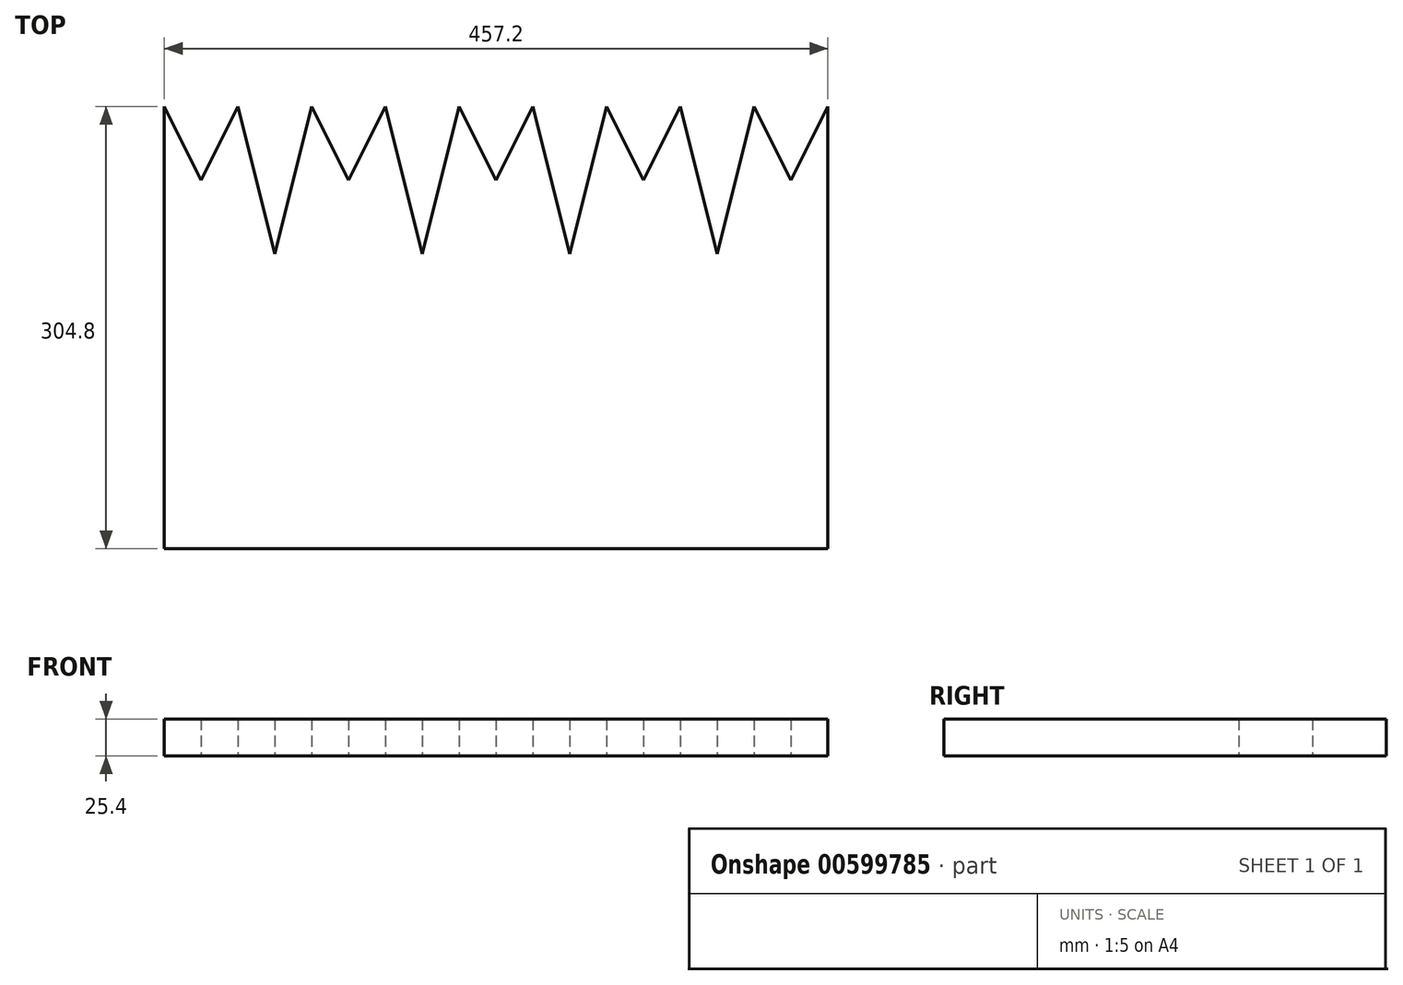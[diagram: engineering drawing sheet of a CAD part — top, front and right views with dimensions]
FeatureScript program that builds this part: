
annotation { "Feature Type Name" : "Feature", "Feature Type Description" : "" }
export const myFeature = defineFeature(function(context is Context, id is Id, definition is map)
    precondition{}
    {
        {
            var Q0;
            Q0=qCreatedBy(makeId("Top.planeOp"),FACE);
            var sketch = newSketch(context, id + "F0", { "sketchPlane" : qUnion([Q0])});
            skLineSegment(sketch, "E0.top", {"start": v(-261.46, -109.7) * mm, "end": v(195.74, -109.7) * mm});
            skLineSegment(sketch, "E0.left", {"start": v(-261.46, 195.1) * mm, "end": v(-261.46, -109.7) * mm});
            skLineSegment(sketch, "E0.right", {"start": v(195.74, 195.1) * mm, "end": v(195.74, -109.7) * mm});
            skLineSegment(sketch, "E1", {"start": v(-261.46, 144.3) * mm, "end": v(195.74, 144.3) * mm, "construction": true});
            skPoint(sketch, "E2", {"position": v(-236.06, 144.3) * mm});
            skPoint(sketch, "E3", {"position": v(-210.66, 144.3) * mm});
            skPoint(sketch, "E4", {"position": v(-185.26, 144.3) * mm});
            skPoint(sketch, "E5", {"position": v(-159.86, 144.3) * mm});
            skPoint(sketch, "E6", {"position": v(-134.46, 144.3) * mm});
            skPoint(sketch, "E7", {"position": v(-109.06, 144.3) * mm});
            skLineSegment(sketch, "E8", {"start": v(-32.86, 195.1) * mm, "end": v(-32.86, -109.7) * mm, "construction": true});
            skPoint(sketch, "E9", {"position": v(-83.66, 144.3) * mm});
            skPoint(sketch, "E10", {"position": v(-58.26, 144.3) * mm});
            skPoint(sketch, "E11.MirrorP", {"position": v(-7.46, 144.3) * mm});
            skPoint(sketch, "E12.MirrorP", {"position": v(17.94, 144.3) * mm});
            skPoint(sketch, "E13.MirrorP", {"position": v(43.34, 144.3) * mm});
            skPoint(sketch, "E14.MirrorP", {"position": v(68.74, 144.3) * mm});
            skPoint(sketch, "E15.MirrorP", {"position": v(94.14, 144.3) * mm});
            skPoint(sketch, "E16.MirrorP", {"position": v(119.54, 144.3) * mm});
            skPoint(sketch, "E17.MirrorP", {"position": v(144.94, 144.3) * mm});
            skPoint(sketch, "E18.MirrorP", {"position": v(170.34, 144.3) * mm});
            skPoint(sketch, "E19", {"position": v(-32.86, 144.3) * mm});
            skLineSegment(sketch, "E20", {"start": v(-261.46, 195.1) * mm, "end": v(-236.06, 144.3) * mm});
            skLineSegment(sketch, "E21", {"start": v(-210.66, 195.1) * mm, "end": v(-236.06, 144.3) * mm});
            skLineSegment(sketch, "E22", {"start": v(-159.86, 195.1) * mm, "end": v(-134.46, 144.3) * mm});
            skLineSegment(sketch, "E23", {"start": v(-134.46, 144.3) * mm, "end": v(-109.06, 195.1) * mm});
            skLineSegment(sketch, "E24", {"start": v(-58.26, 195.1) * mm, "end": v(-32.86, 144.3) * mm});
            skLineSegment(sketch, "E25", {"start": v(-32.86, 144.3) * mm, "end": v(-7.46, 195.1) * mm});
            skLineSegment(sketch, "E26", {"start": v(43.34, 195.1) * mm, "end": v(68.74, 144.3) * mm});
            skLineSegment(sketch, "E27", {"start": v(68.74, 144.3) * mm, "end": v(94.14, 195.1) * mm});
            skLineSegment(sketch, "E28", {"start": v(144.94, 195.1) * mm, "end": v(170.34, 144.3) * mm});
            skLineSegment(sketch, "E29", {"start": v(170.34, 144.3) * mm, "end": v(195.74, 195.1) * mm});
            skLineSegment(sketch, "E30", {"start": v(-261.46, 93.5) * mm, "end": v(195.74, 93.5) * mm, "construction": true});
            skLineSegment(sketch, "E31", {"start": v(-210.66, 195.1) * mm, "end": v(-185.26, 93.5) * mm});
            skLineSegment(sketch, "E32", {"start": v(-185.26, 93.5) * mm, "end": v(-159.86, 195.1) * mm});
            skLineSegment(sketch, "E33", {"start": v(-109.06, 195.1) * mm, "end": v(-83.66, 93.5) * mm});
            skLineSegment(sketch, "E34", {"start": v(-83.66, 93.5) * mm, "end": v(-58.26, 195.1) * mm});
            skLineSegment(sketch, "E35", {"start": v(-7.46, 195.1) * mm, "end": v(17.94, 93.5) * mm});
            skLineSegment(sketch, "E36", {"start": v(17.94, 93.5) * mm, "end": v(43.34, 195.1) * mm});
            skLineSegment(sketch, "E37", {"start": v(94.14, 195.1) * mm, "end": v(119.54, 93.5) * mm});
            skLineSegment(sketch, "E38", {"start": v(119.54, 93.5) * mm, "end": v(144.94, 195.1) * mm});
            skSolve(sketch);
        }
        {
            var Q0;
            Q0=makeQuery(id+"F0.imprint","IMPRINT",FACE,{"disambiguationData":[TD([[makeQuery(id+"F0.imprint","IMPRINT",EDGE,{"derivedFrom":sQuery(id+"F0.wireOp",EDGE,"E0.top")}),1.0]])]});
            extrude(context, id + "F1", {"entities" : qUnion([Q0]), "depth" : 25.4 * mm, "offsetDistance" : 25.4 * mm});
        }
    });
